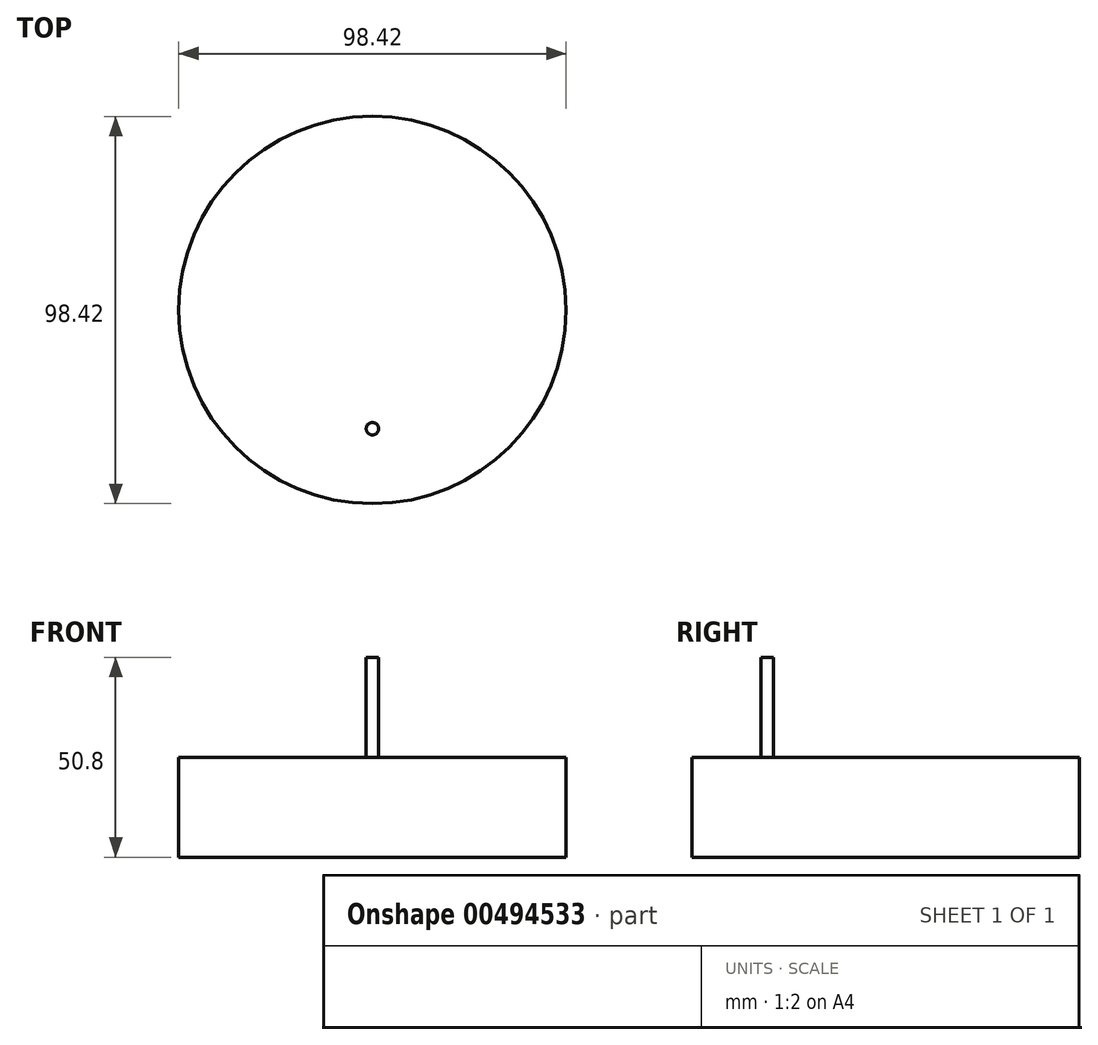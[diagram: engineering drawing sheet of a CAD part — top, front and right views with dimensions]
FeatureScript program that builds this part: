
annotation { "Feature Type Name" : "Feature", "Feature Type Description" : "" }
export const myFeature = defineFeature(function(context is Context, id is Id, definition is map)
    precondition{}
    {
        {
            var Q0;
            Q0=qCreatedBy(makeId("Top.planeOp"),FACE);
            var sketch = newSketch(context, id + "F0", { "sketchPlane" : qUnion([Q0])});
            skCircle(sketch, "E0", {"center": v(0, 0) * mm, "radius": 49.21 * mm});
            skSolve(sketch);
        }
        {
            var Q0;
            Q0=makeQuery(id+"F0.imprint","IMPRINT",FACE,{"disambiguationData":[TD([[makeQuery(id+"F0.imprint","IMPRINT",EDGE,{"derivedFrom":sQuery(id+"F0.wireOp",EDGE,"E0")}),1.0]])]});
            extrude(context, id + "F1", {"entities" : qUnion([Q0]), "oppositeDirection" : true, "depth" : 25.4 * mm, "offsetDistance" : 25.4 * mm});
        }
        {
            var Q0;
            Q0=makeQuery(id+"F1.opExtrude","CAP_FACE",FACE,{"disambiguationData":[OSD([sQuery(id+"F0.wireOp",EDGE,"E0")])],"isStart":true});
            var sketch = newSketch(context, id + "F2", { "sketchPlane" : qUnion([Q0])});
            skCircle(sketch, "E1", {"center": v(0, -30.16) * mm, "radius": 1.59 * mm});
            skSolve(sketch);
        }
        {
            var Q0;
            Q0=makeQuery(id+"F2.imprint","IMPRINT",FACE,{"disambiguationData":[TD([[makeQuery(id+"F2.imprint","IMPRINT",EDGE,{"derivedFrom":sQuery(id+"F2.wireOp",EDGE,"E1")}),1.0]])]});
            extrude(context, id + "F3", {"entities" : qUnion([Q0]), "operationType" : NewBodyOperationType.ADD, "depth" : 25.4 * mm, "offsetDistance" : 25.4 * mm});
        }
    });
